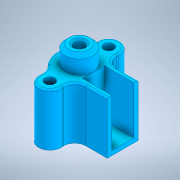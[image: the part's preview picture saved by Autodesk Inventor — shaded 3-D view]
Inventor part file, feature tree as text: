
AUTODESK INVENTOR PART (.ipt)
format: ipt  version: 2020 (Build 240168000, 168)  size: 230,912 bytes
history: native  units: mm
features: sketch x5, fillet x3, extrude x2, revolve x1, chamfer x1
ambient origin geometry x8: Origin, YZ Plane, XZ Plane, XY Plane, X Axis, Y Axis, Z Axis, Center Point
bodies: Solid1 (feature_tree)
feature tree (12):
  revolve  "Revolution1"  [1 undecoded]
  chamfer  "Chamfer1"  Distance=0.5mm Angle=45.0deg
  extrude  "Extrusion3"  Depth=8.0mm
  fillet  "Fillet1"  Radius=12.0mm
  sketch  "Sketch7"  dims[d20=3.8mm d21=0.5mm d22=2.0mm d23=45.0deg]
  sketch  "Sketch8"  dims[d24=6.0mm d26=8.0mm d27=12.0mm]
  extrude  "Extrusion4"  Depth=14.2mm TaperAngle=0.0deg
  fillet  "Fillet4"  Radius=4.0mm
  fillet  "Fillet5"  Radius=2.0mm
  sketch  "Sketch1"  dims[d1=1.4mm d8=1.0mm]
  sketch  "Sketch6"  dims[d9=90.0deg]
  sketch  "Sketch10"  dims[d28=2.7mm d29=14.2mm d30=0.0mm d31=4.0mm d33=2.0mm d34=8.4mm d35=11.8mm d39=6.0mm d40=1.2mm d41=13.0mm d42=8.0mm d43=0.0mm d44=3.0mm d45=0.5mm d46=19.0mm]
note: 1 required parameter value undecoded (feature->parameter linkage not recoverable at this tier; creation-order binding heuristic only, values carry confidence <= 0.55)
